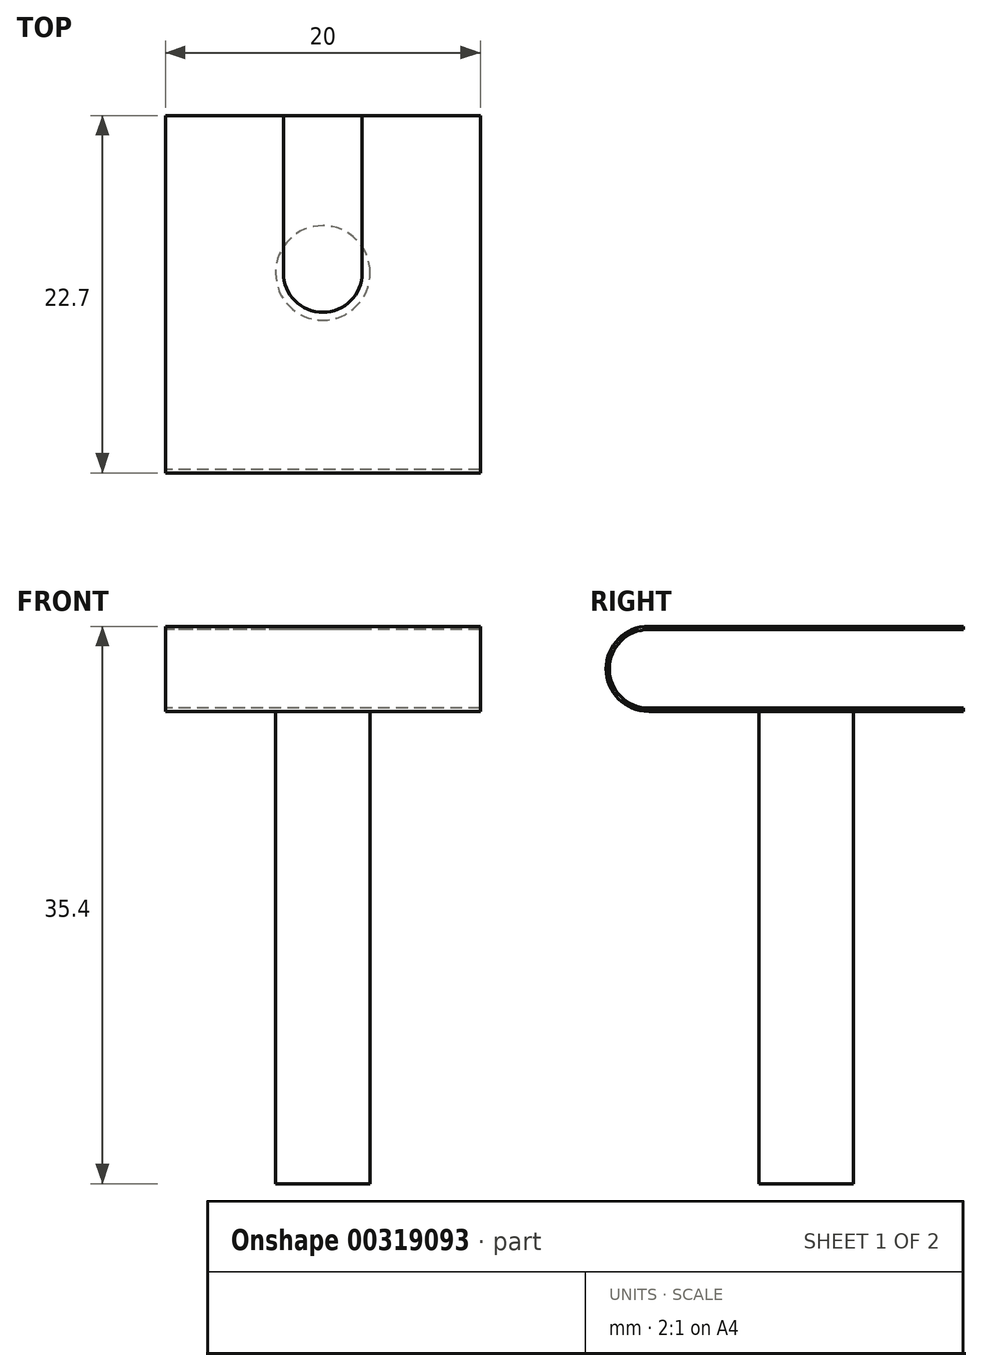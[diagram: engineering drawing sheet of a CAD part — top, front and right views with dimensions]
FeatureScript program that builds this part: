
annotation { "Feature Type Name" : "Feature", "Feature Type Description" : "" }
export const myFeature = defineFeature(function(context is Context, id is Id, definition is map)
    precondition{}
    {
        {
            var Q0;
            Q0=qCreatedBy(makeId("Right.planeOp"),FACE);
            var sketch = newSketch(context, id + "F0", { "sketchPlane" : qUnion([Q0])});
            skLineSegment(sketch, "E0", {"start": v(10, 5) * mm, "end": v(-10, 5) * mm});
            skArc(sketch, "E1", {"start": v(-10, 5) * mm, "mid": v(-12.5, 2.5) * mm, "end": v(-10, 0) * mm});
            skLineSegment(sketch, "E2", {"start": v(-10, 0) * mm, "end": v(10, 0) * mm});
            skLineSegment(sketch, "E3", {"start": v(10, 5) * mm, "end": v(10, 5.2) * mm});
            skLineSegment(sketch, "E4", {"start": v(10, 5.2) * mm, "end": v(-10, 5.2) * mm});
            skArc(sketch, "E5", {"start": v(-10, 5.2) * mm, "mid": v(-12.7, 2.5) * mm, "end": v(-10, -0.2) * mm});
            skLineSegment(sketch, "E6", {"start": v(10, 0) * mm, "end": v(10, -0.2) * mm});
            skLineSegment(sketch, "E7", {"start": v(10, -0.2) * mm, "end": v(-10, -0.2) * mm});
            skSolve(sketch);
        }
        {
            var Q0;
            Q0 = qSketchRegion(id + "F0", true);
            extrude(context, id + "F1", {"entities" : qUnion([Q0]), "endBound" : BoundingType.SYMMETRIC, "depth" : 20 * mm});
        }
        {
            var Q0;
            Q0=makeQuery(id+"F1.opExtrude","SWEPT_FACE",FACE,{"disambiguationData":[OSD([sQuery(id+"F0.wireOp",EDGE,"E4")])]});
            var sketch = newSketch(context, id + "F2", { "sketchPlane" : qUnion([Q0])});
            skArc(sketch, "E8", {"start": v(-2.5, 0) * mm, "mid": v(0, -2.5) * mm, "end": v(2.5, 0) * mm});
            skPoint(sketch, "E8.startSnap0", {"position": v(-10, 0) * mm});
            skLineSegment(sketch, "E9", {"start": v(-2.5, 0) * mm, "end": v(-2.5, 10) * mm});
            skLineSegment(sketch, "E10", {"start": v(-2.5, 10) * mm, "end": v(2.5, 10) * mm});
            skLineSegment(sketch, "E11", {"start": v(2.5, 10) * mm, "end": v(2.5, 0) * mm});
            skSolve(sketch);
        }
        {
            var Q0;
            Q0 = qSketchRegion(id + "F2", true);
            extrude(context, id + "F3", {"entities" : qUnion([Q0]), "operationType" : NewBodyOperationType.REMOVE, "endBound" : BoundingType.UP_TO_NEXT, "oppositeDirection" : true, "depth" : 25 * mm});
        }
        {
            var Q0;
            Q0=makeQuery(id+"F1.opExtrude","SWEPT_FACE",FACE,{"disambiguationData":[OSD([sQuery(id+"F0.wireOp",EDGE,"E7")])]});
            var sketch = newSketch(context, id + "F4", { "sketchPlane" : qUnion([Q0])});
            skCircle(sketch, "E12", {"center": v(0, 0) * mm, "radius": 3 * mm});
            skSolve(sketch);
        }
        {
            var Q0;
            Q0 = qSketchRegion(id + "F4", true);
            extrude(context, id + "F5", {"entities" : qUnion([Q0]), "operationType" : NewBodyOperationType.ADD, "depth" : 30 * mm});
        }
    });
